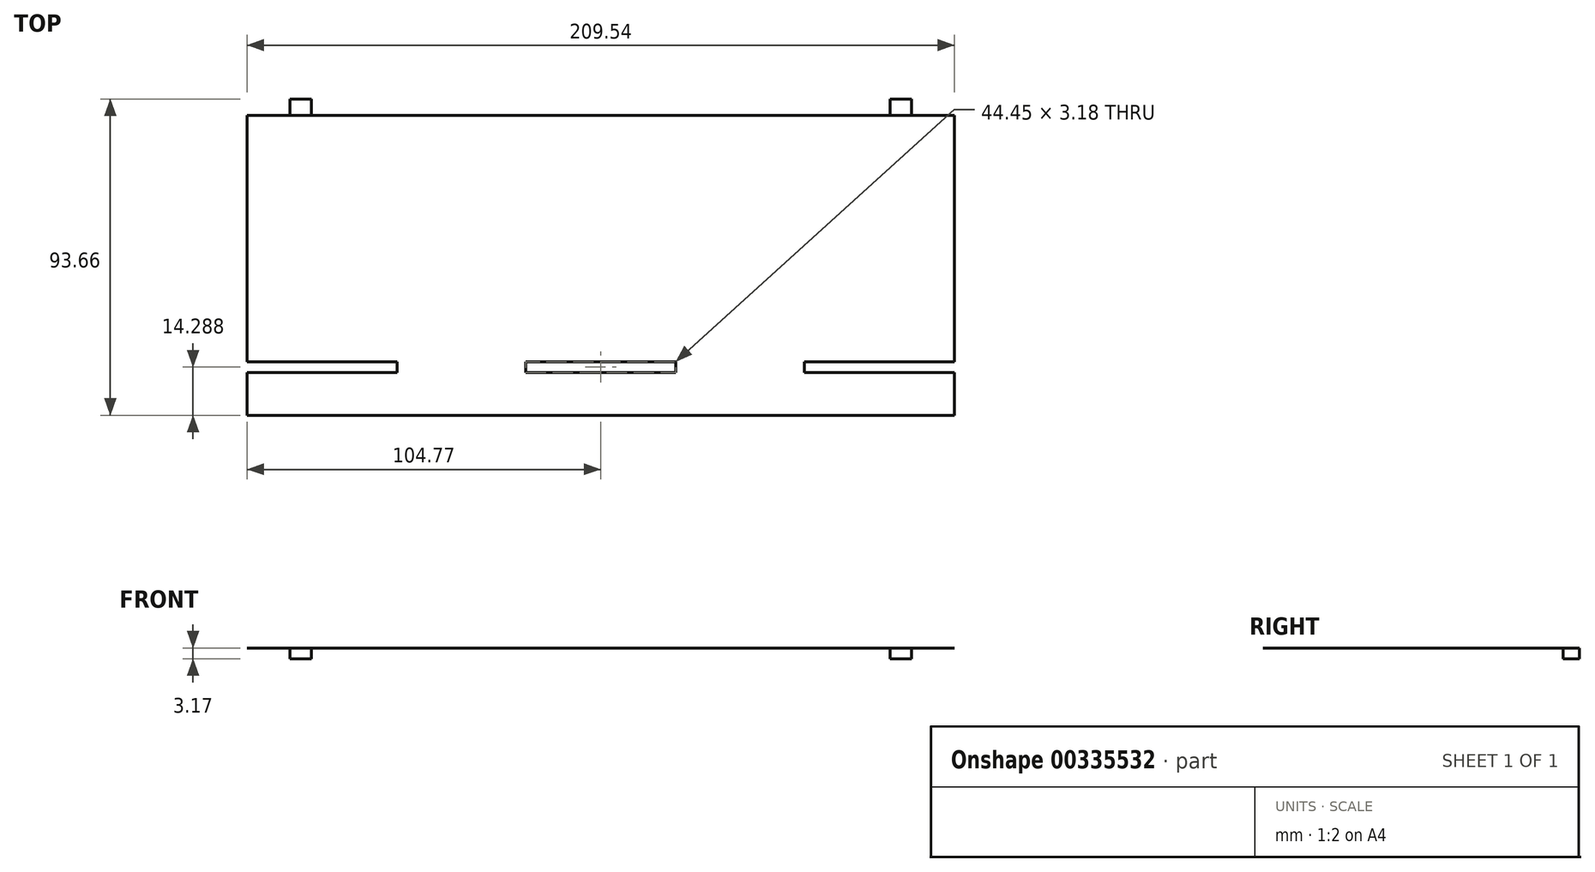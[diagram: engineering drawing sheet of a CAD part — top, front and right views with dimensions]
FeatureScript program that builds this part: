
annotation { "Feature Type Name" : "Feature", "Feature Type Description" : "" }
export const myFeature = defineFeature(function(context is Context, id is Id, definition is map)
    precondition{}
    {
        {
            var Q0;
            Q0=qCreatedBy(makeId("Top.planeOp"),FACE);
            var sketch = newSketch(context, id + "F0", { "sketchPlane" : qUnion([Q0])});
            skLineSegment(sketch, "E0.bottom", {"start": v(104.78, -44.45) * mm, "end": v(-104.77, -44.45) * mm});
            skLineSegment(sketch, "E0.top", {"start": v(104.77, 44.45) * mm, "end": v(-104.78, 44.45) * mm});
            skLineSegment(sketch, "E0.left", {"start": v(104.78, -44.45) * mm, "end": v(104.77, 44.45) * mm});
            skLineSegment(sketch, "E0.right", {"start": v(-104.77, -44.45) * mm, "end": v(-104.78, 44.45) * mm});
            skPoint(sketch, "E0.middle", {"position": v(0, 0) * mm});
            skSolve(sketch);
        }
        {
            var Q0;
            Q0=makeQuery(id+"F0.imprint","IMPRINT",FACE,{"disambiguationData":[TD([[makeQuery(id+"F0.imprint","IMPRINT",EDGE,{"derivedFrom":sQuery(id+"F0.wireOp",EDGE,"E0.bottom")}),-1.0]])]});
            extrude(context, id + "F1", {"entities" : qUnion([Q0]), "depth" : 1 / 203.2 * mm});
        }
        {
            var Q0;
            Q0=makeQuery(id+"F1.opExtrude","CAP_FACE",FACE,{"disambiguationData":[OSD([sQuery(id+"F0.wireOp",EDGE,"E0.bottom"),sQuery(id+"F0.wireOp",EDGE,"E0.top"),sQuery(id+"F0.wireOp",EDGE,"E0.left"),sQuery(id+"F0.wireOp",EDGE,"E0.right")])],"isStart":false});
            var sketch = newSketch(context, id + "F2", { "sketchPlane" : qUnion([Q0])});
            skLineSegment(sketch, "E1.bottom", {"start": v(-104.77, -28.58) * mm, "end": v(-60.32, -28.58) * mm});
            skLineSegment(sketch, "E1.top", {"start": v(-104.77, -31.75) * mm, "end": v(-60.32, -31.75) * mm});
            skLineSegment(sketch, "E1.left", {"start": v(-104.77, -28.57) * mm, "end": v(-104.77, -31.75) * mm});
            skLineSegment(sketch, "E1.right", {"start": v(-60.32, -28.57) * mm, "end": v(-60.32, -31.75) * mm});
            skLineSegment(sketch, "E2.right", {"start": v(104.77, -28.57) * mm, "end": v(104.77, -31.75) * mm});
            skLineSegment(sketch, "E3.bottom", {"start": v(60.33, -28.57) * mm, "end": v(104.78, -28.57) * mm});
            skLineSegment(sketch, "E3.top", {"start": v(60.33, -31.75) * mm, "end": v(104.78, -31.75) * mm});
            skLineSegment(sketch, "E3.left", {"start": v(60.33, -28.57) * mm, "end": v(60.33, -31.75) * mm});
            skLineSegment(sketch, "E3.right", {"start": v(104.78, -28.57) * mm, "end": v(104.78, -31.75) * mm});
            skLineSegment(sketch, "E4.bottom", {"start": v(22.23, -31.75) * mm, "end": v(-22.23, -31.75) * mm});
            skLineSegment(sketch, "E4.top", {"start": v(22.23, -28.58) * mm, "end": v(-22.23, -28.58) * mm});
            skLineSegment(sketch, "E4.left", {"start": v(22.23, -31.75) * mm, "end": v(22.23, -28.58) * mm});
            skLineSegment(sketch, "E4.right", {"start": v(-22.23, -31.75) * mm, "end": v(-22.23, -28.58) * mm});
            skPoint(sketch, "E4.middle", {"position": v(0, -30.16) * mm});
            skSolve(sketch);
        }
        {
            var Q0;
            Q0=qSketchRegion(id+"F2",true);
            extrude(context, id + "F3", {"entities" : qUnion([Q0]), "operationType" : NewBodyOperationType.REMOVE, "oppositeDirection" : true, "depth" : 25.4 * mm});
        }
        {
            var Q0;
            Q0=makeQuery(id+"F1.opExtrude","CAP_FACE",FACE,{"disambiguationData":[OSD([sQuery(id+"F0.wireOp",EDGE,"E0.bottom"),sQuery(id+"F0.wireOp",EDGE,"E0.top"),sQuery(id+"F0.wireOp",EDGE,"E0.left"),sQuery(id+"F0.wireOp",EDGE,"E0.right")])],"isStart":false});
            var sketch = newSketch(context, id + "F4", { "sketchPlane" : qUnion([Q0])});
            skLineSegment(sketch, "E5.bottom", {"start": v(-92.08, 44.45) * mm, "end": v(-85.73, 44.45) * mm});
            skLineSegment(sketch, "E5.top", {"start": v(-92.08, 49.21) * mm, "end": v(-85.73, 49.21) * mm});
            skLineSegment(sketch, "E5.left", {"start": v(-85.73, 44.45) * mm, "end": v(-85.73, 49.21) * mm});
            skLineSegment(sketch, "E5.right", {"start": v(-92.08, 44.45) * mm, "end": v(-92.08, 49.21) * mm});
            skLineSegment(sketch, "E6.MirrorCS", {"start": v(92.08, 44.45) * mm, "end": v(92.08, 49.21) * mm});
            skLineSegment(sketch, "E7.MirrorCS", {"start": v(85.73, 44.45) * mm, "end": v(85.73, 49.21) * mm});
            skLineSegment(sketch, "E8.MirrorCS", {"start": v(92.08, 49.21) * mm, "end": v(85.73, 49.21) * mm});
            skLineSegment(sketch, "E9.MirrorCS", {"start": v(92.08, 44.45) * mm, "end": v(85.73, 44.45) * mm});
            skSolve(sketch);
        }
        {
            var Q0;
            Q0 = qSketchRegion(id + "F4", true);
            extrude(context, id + "F5", {"entities" : qUnion([Q0]), "operationType" : NewBodyOperationType.ADD, "oppositeDirection" : true, "depth" : 3.17 * mm});
        }
    });
